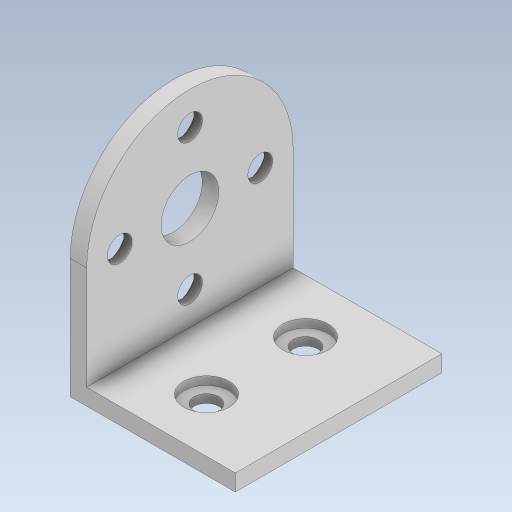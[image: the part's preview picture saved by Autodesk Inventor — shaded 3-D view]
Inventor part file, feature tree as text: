
AUTODESK INVENTOR PART (.ipt)
format: ipt  version: 2023.5 (Build 275446000, 446)  size: 188,416 bytes
history: native  units: in
note: dims shown in document units (in); Inventor stores cm internally (conversion verified against a paired STEP export)
features: extrude x7, sketch x3
ambient origin geometry x8: Origin, YZ Plane, XZ Plane, XY Plane, X Axis, Y Axis, Z Axis, Center Point
bodies: Solid1 (feature_tree)
feature tree (10):
  sketch  "Sketch1"  dims[d0=0.7874in d1=0.9843in]
  extrude  "Extrusion1"  Depth=0.9843in
  extrude  "Extrusion2"  Depth=0.0787in
  extrude  "Extrusion3"  Depth=0.2362in
  extrude  "Extrusion4"  Depth=0.0787in TaperAngle=0.0deg
  sketch  "Sketch3"  dims[d4=0.2165in d5=0.2362in d6=0.0787in d7=0.0in d8=0.0394in d9=0.0in d10=1.063in d11=0.0in d12=0.9843in d13=0.0787in d14=0.0in d15=0.1181in d16=0.2165in d17=0.3346in d18=0.0787in d19=0.0in d20=0.0394in d21=0.0in d22=0.2756in d23=0.0787in d24=0.0in d25=0.1181in d26=0.2165in d27=0.3346in d28=0.1181in d29=0.2165in d30=0.3346in]
  extrude  "Extrusion5"  Depth=0.0394in TaperAngle=0.0deg
  extrude  "Extrusion6"  Depth=0.0787in TaperAngle=0.0deg
  extrude  "Extrusion7"  Depth=0.9843in
  sketch  "Sketch2"  dims[d2=0.0787in d3=0.1181in]
